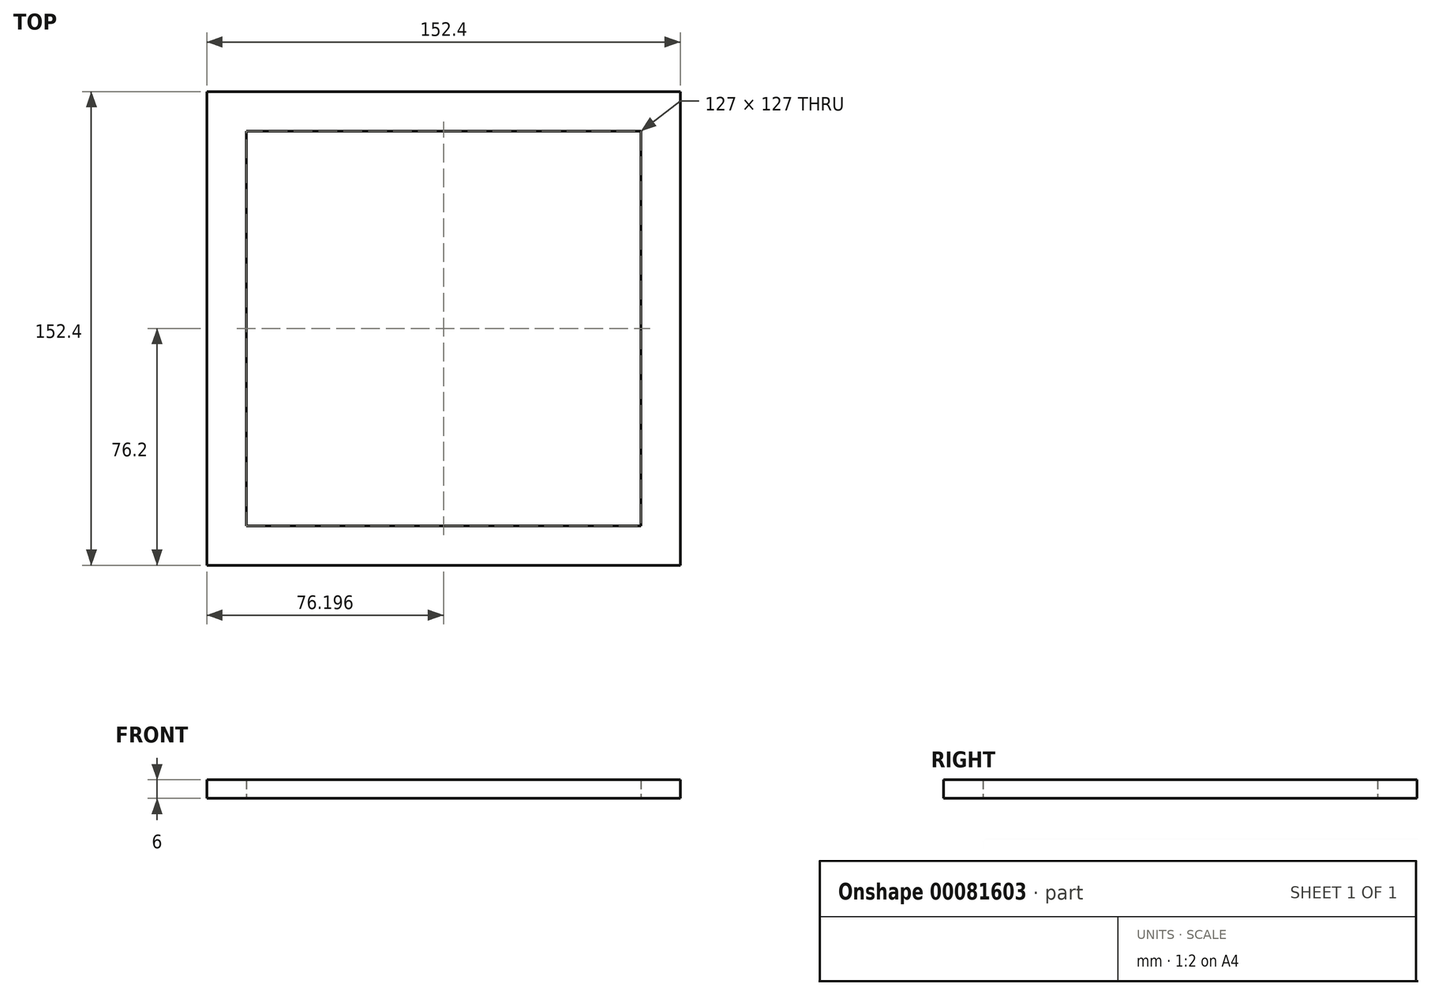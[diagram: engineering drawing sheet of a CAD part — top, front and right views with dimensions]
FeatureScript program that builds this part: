
annotation { "Feature Type Name" : "Feature", "Feature Type Description" : "" }
export const myFeature = defineFeature(function(context is Context, id is Id, definition is map)
    precondition{}
    {
        {
            assignVariable(context, id + "F0", {"name" : "w", "anyValue" : .5});
        }
        {
            var Q0;
            Q0=qCreatedBy(makeId("Top.planeOp"),FACE);
            var sketch = newSketch(context, id + "F1", { "sketchPlane" : qUnion([Q0])});
            skLineSegment(sketch, "E0.bottom", {"start": v(-63.2, 71.44) * mm, "end": v(63.8, 71.44) * mm});
            skLineSegment(sketch, "E0.top", {"start": v(-63.2, -55.56) * mm, "end": v(63.8, -55.56) * mm});
            skLineSegment(sketch, "E0.left", {"start": v(-63.2, 71.44) * mm, "end": v(-63.2, -55.56) * mm});
            skLineSegment(sketch, "E0.right", {"start": v(63.8, 71.44) * mm, "end": v(63.8, -55.56) * mm});
            skLineSegment(sketch, "E1.0", {"start": v(-75.9, 84.14) * mm, "end": v(-75.9, -68.26) * mm});
            skLineSegment(sketch, "E1.1", {"start": v(-75.9, 84.14) * mm, "end": v(76.5, 84.14) * mm});
            skLineSegment(sketch, "E1.2", {"start": v(76.5, 84.14) * mm, "end": v(76.5, -68.26) * mm});
            skLineSegment(sketch, "E1.3", {"start": v(-75.9, -68.26) * mm, "end": v(76.5, -68.26) * mm});
            skSolve(sketch);
        }
        {
            var Q0;
            Q0 = qSketchRegion(id + "F1", true);
            extrude(context, id + "F2", {"entities" : qUnion([Q0]), "depth" : (getVariable(context, 'w') * 2 + 5) * mm});
        }
    });
